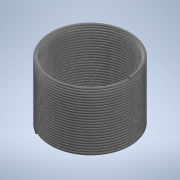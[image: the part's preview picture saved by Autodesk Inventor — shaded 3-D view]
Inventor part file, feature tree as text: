
AUTODESK INVENTOR PART (.ipt)
format: ipt  version: 2020 (Build 240168000, 168)  size: 2,273,280 bytes
history: native  units: mm
features: helix x1, sketch x1
ambient origin geometry x8: Origin, YZ Plane, XZ Plane, XY Plane, X Axis, Y Axis, Z Axis, Center Point
bodies: Solid1 (feature_tree)
feature tree (2):
  helix  "Coil1"  [1 undecoded]
  sketch  "Sketch1"  dims[d2=2.0mm d3=50.0mm d4=250.0mm d5=0.0mm d6=150.0deg d7=90.0deg d8=0.0mm d9=0.0mm]
note: 1 required parameter value undecoded (feature->parameter linkage not recoverable at this tier; creation-order binding heuristic only, values carry confidence <= 0.55)
